# Revit family: Primo KS
name_source: partatom
category: Мебель
revit_build: Autodesk Revit 2017 (Build: 20160225_1515(x64)
units: mm (PartAtom-declared; Revit-internal decimal feet)

## family parameters
Всегда вертикально = Да
На основе рабочей плоскости = Нет
Общий = Нет
При загрузке вырезать с полостями = Нет
Точка расчета площади = Нет

## types (6) — shared parameters
Legs Material = Aluminum
Seat Material = Skandiform Fabric Orange
Изготовитель = Skandiform AB
Ключевая пометка = XBF.2
Комментарии к типоразмеру = Created by Astacus AB

## per-type parameters (varying)
| type | 192,193 | Leg Type | Seat Type | URL |
| KS-132 | Нет | Legs 132,3&192,3 | S : Seat | http://file-system.ru |
| KS-133 | Нет | Legs 132,3&192,3 | H : Seat | http://www.skandiform.com |
| KS-183 | Нет | Legs 182,3 | H : Seat | http://www.skandiform.com |
| KS-192 | Да | Legs 132,3&192,3 | S : Seat | http://www.skandiform.com |
| KS-193 | Да | Legs 132,3&192,3 | H : Seat | http://www.skandiform.com |
| KS-182 | Нет | Legs 182,3 | S : Seat | http://www.skandiform.com |

note: column(s) folded — value = type name in every type: Группа модели

## geometry (parser evidence)
native form markers: Blend x10, Sweep x14
no freeform markers — native parametric forms only
